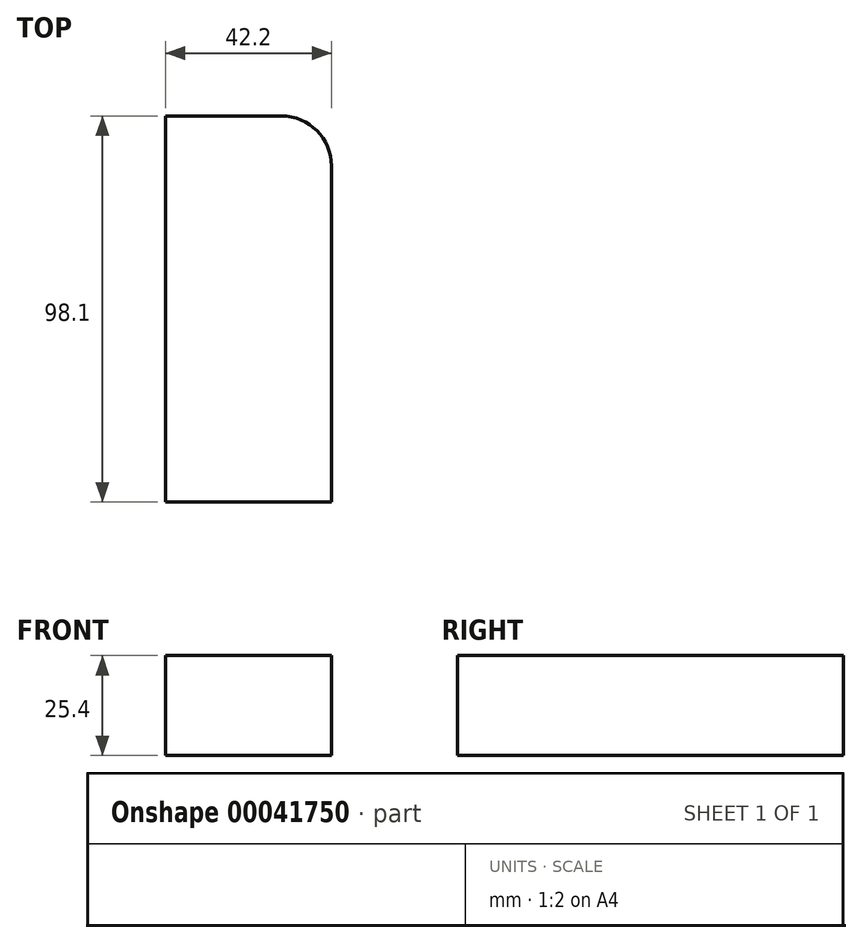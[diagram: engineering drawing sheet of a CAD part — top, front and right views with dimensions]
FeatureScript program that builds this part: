
annotation { "Feature Type Name" : "Feature", "Feature Type Description" : "" }
export const myFeature = defineFeature(function(context is Context, id is Id, definition is map)
    precondition{}
    {
        {
            var Q0;
            Q0=qCreatedBy(makeId("Top.planeOp"),FACE);
            var sketch = newSketch(context, id + "F0", { "sketchPlane" : qUnion([Q0])});
            skLineSegment(sketch, "E0.rect.bottom", {"start": v(-21.1, -49.05) * mm, "end": v(21.1, -49.05) * mm});
            skLineSegment(sketch, "E0.rect.top", {"start": v(-21.1, 49.05) * mm, "end": v(8.4, 49.05) * mm});
            skLineSegment(sketch, "E0.rect.left", {"start": v(-21.1, -49.05) * mm, "end": v(-21.1, 49.05) * mm});
            skLineSegment(sketch, "E0.rect.right", {"start": v(21.1, -49.05) * mm, "end": v(21.1, 36.35) * mm});
            skPoint(sketch, "E0.rect.middle", {"position": v(0, 0) * mm});
            skPoint(sketch, "E1.visualSharp", {"position": v(21.1, 49.05) * mm});
            skArc(sketch, "E1.filletArc", {"start": v(21.1, 36.35) * mm, "mid": v(17.38, 45.33) * mm, "end": v(8.4, 49.05) * mm});
            skSolve(sketch);
        }
        {
            var Q0;
            Q0 = qSketchRegion(id + "F0", true);
            extrude(context, id + "F1", {"entities" : qUnion([Q0]), "depth" : 25.4 * mm});
        }
    });
